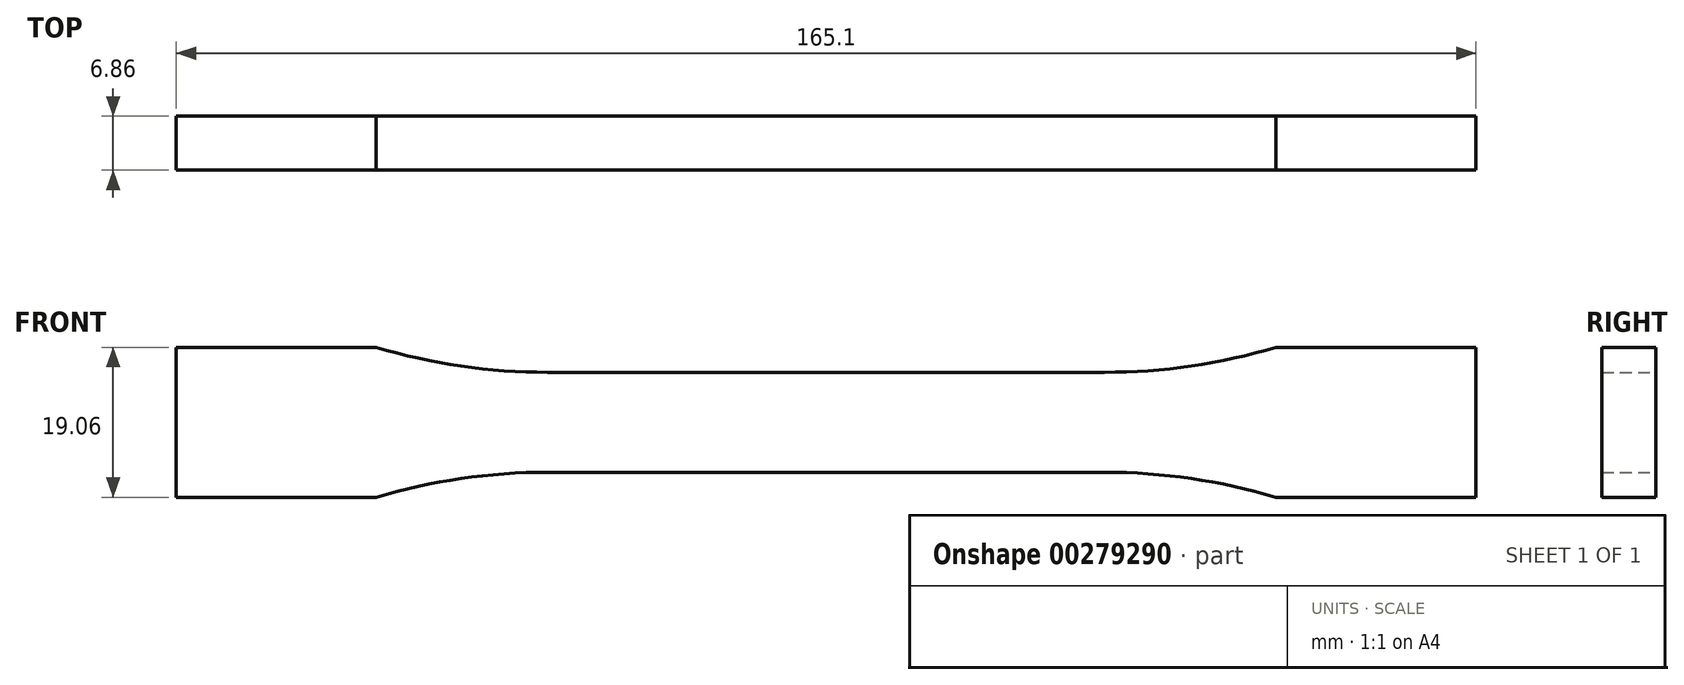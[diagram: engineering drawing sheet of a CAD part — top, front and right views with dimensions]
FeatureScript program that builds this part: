
annotation { "Feature Type Name" : "Feature", "Feature Type Description" : "" }
export const myFeature = defineFeature(function(context is Context, id is Id, definition is map)
    precondition{}
    {
        {
            var Q0;
            Q0=qCreatedBy(makeId("Front.planeOp"),FACE);
            var sketch = newSketch(context, id + "F0", { "sketchPlane" : qUnion([Q0])});
            skLineSegment(sketch, "E0", {"start": v(0, 6.35) * mm, "end": v(35.38, 6.35) * mm});
            skArc(sketch, "E1", {"start": v(35.38, 6.35) * mm, "mid": v(46.38, 7.15) * mm, "end": v(57.15, 9.53) * mm});
            skLineSegment(sketch, "E2", {"start": v(57.15, 9.53) * mm, "end": v(82.55, 9.53) * mm});
            skArc(sketch, "E3.MirrorCS", {"start": v(35.38, -6.35) * mm, "mid": v(46.38, -7.15) * mm, "end": v(57.15, -9.53) * mm});
            skLineSegment(sketch, "E4.MirrorCS", {"start": v(0, -6.35) * mm, "end": v(35.38, -6.35) * mm});
            skLineSegment(sketch, "E5.MirrorCS", {"start": v(57.15, -9.53) * mm, "end": v(82.55, -9.53) * mm});
            skLineSegment(sketch, "E6.MirrorCS", {"start": v(0, -6.35) * mm, "end": v(-35.38, -6.35) * mm});
            skLineSegment(sketch, "E7.MirrorCS", {"start": v(-57.15, -9.53) * mm, "end": v(-82.55, -9.53) * mm});
            skArc(sketch, "E8.MirrorCS", {"start": v(-35.38, -6.35) * mm, "mid": v(-46.38, -7.15) * mm, "end": v(-57.15, -9.53) * mm});
            skLineSegment(sketch, "E9.MirrorCS", {"start": v(-57.15, 9.53) * mm, "end": v(-82.55, 9.53) * mm});
            skLineSegment(sketch, "E10.MirrorCS", {"start": v(0, 6.35) * mm, "end": v(-35.38, 6.35) * mm});
            skArc(sketch, "E11.MirrorCS", {"start": v(-35.38, 6.35) * mm, "mid": v(-46.38, 7.15) * mm, "end": v(-57.15, 9.53) * mm});
            skLineSegment(sketch, "E12", {"start": v(-82.55, 9.53) * mm, "end": v(-82.55, -9.53) * mm});
            skLineSegment(sketch, "E13", {"start": v(82.55, 9.53) * mm, "end": v(82.55, -9.53) * mm});
            skSolve(sketch);
        }
        {
            var Q0;
            Q0=makeQuery(id+"F0.imprint","IMPRINT",FACE,{"disambiguationData":[TD([[makeQuery(id+"F0.imprint","IMPRINT",EDGE,{"derivedFrom":sQuery(id+"F0.wireOp",EDGE,"E0")}),-1.0]])]});
            extrude(context, id + "F1", {"entities" : qUnion([Q0]), "depth" : 6.86 * mm});
        }
    });
